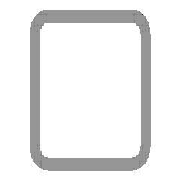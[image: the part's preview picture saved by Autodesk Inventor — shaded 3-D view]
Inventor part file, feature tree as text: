
AUTODESK INVENTOR PART (.ipt)
format: ipt  version: 2025.3 (Build 293356000, 356)  size: 141,824 bytes
history: native  units: mm (DEFAULTED — no unit token found)
features: other x4, plane x2, split x1, sketch x1
ambient origin geometry x8: Origin, YZ Plane, XZ Plane, XY Plane, X Axis, Y Axis, Z Axis, Center Point
bodies: Solid1 (feature_tree), Body (feature_tree)
feature tree (8):
  parser-record x1  (decoder bookkeeping rows leaked as tree rows — omitted from the tree; the rows remain in map.json)
  other  "Driven Length"
  other  "Start Plane"
  other  "End Plane"
  plane  "Work Plane4"
  split  "Split1"
  sketch  "Sketch3"  dims[d3=2446.612931mm d4=0.0mm d7=6.0mm d9=80.0mm d11=80.0mm d12=3.0mm d13=-0.0mm d14=2446.612931mm d15=40.0mm d16=40.0mm d17=90.0deg d18=2446.612931mm]
  plane  "Work Plane3"
